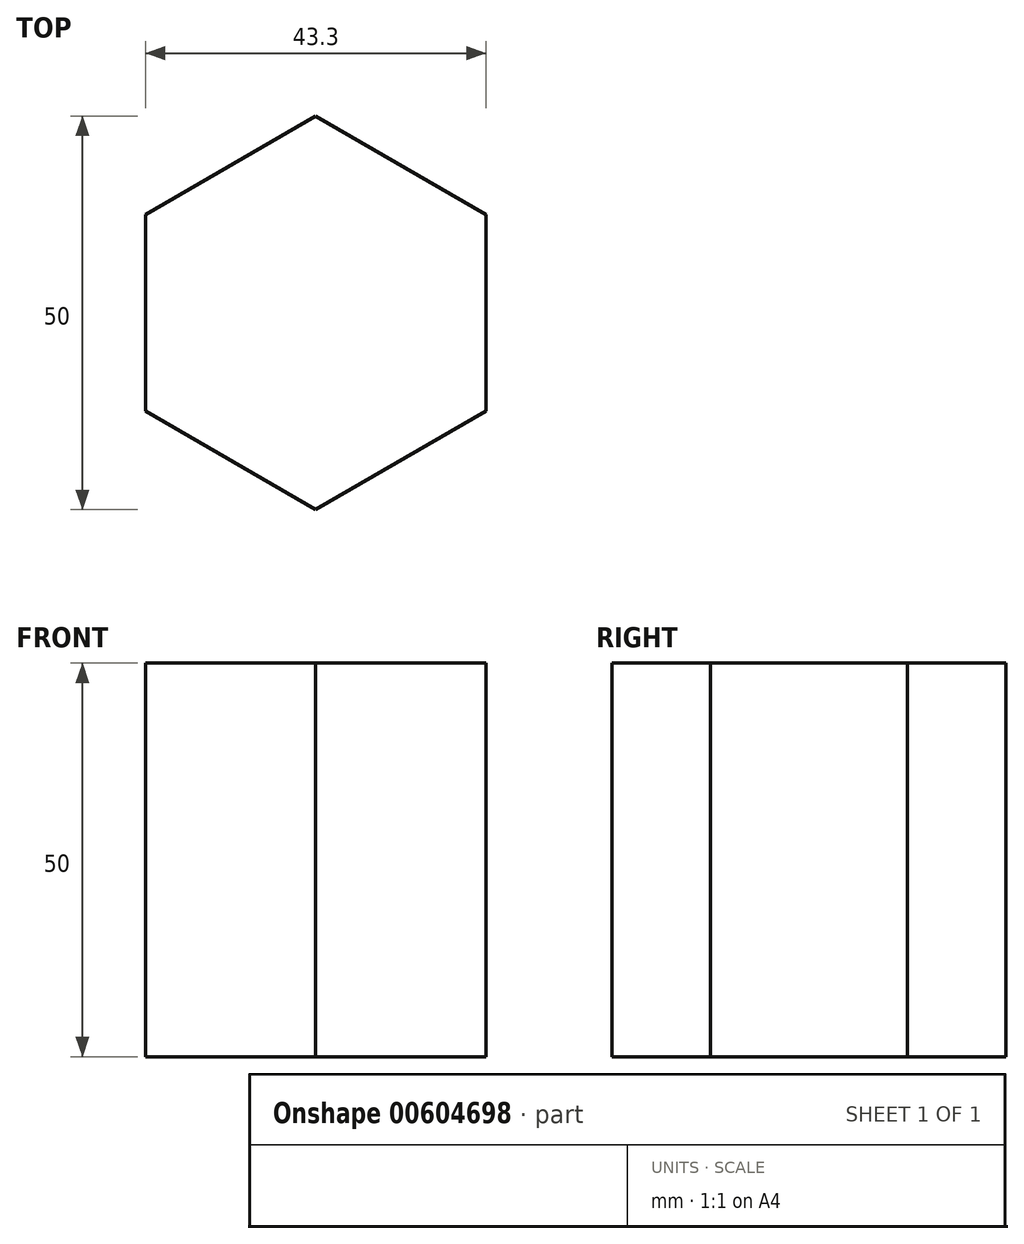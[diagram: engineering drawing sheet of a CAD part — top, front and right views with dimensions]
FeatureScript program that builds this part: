
annotation { "Feature Type Name" : "Feature", "Feature Type Description" : "" }
export const myFeature = defineFeature(function(context is Context, id is Id, definition is map)
    precondition{}
    {
        {
            var Q0;
            Q0=qCreatedBy(makeId("Top.planeOp"),FACE);
            var sketch = newSketch(context, id + "F0", { "sketchPlane" : qUnion([Q0])});
            skCircle(sketch, "E0.cCircle", {"center": v(0, 0) * mm, "radius": 25 * mm, "construction": true});
            skLineSegment(sketch, "E0.0", {"start": v(0, -25) * mm, "end": v(-21.65, -12.5) * mm});
            skLineSegment(sketch, "E0.1", {"start": v(-21.65, -12.5) * mm, "end": v(-21.65, 12.5) * mm});
            skLineSegment(sketch, "E0.2", {"start": v(-21.65, 12.5) * mm, "end": v(0, 25) * mm});
            skLineSegment(sketch, "E0.3", {"start": v(0, 25) * mm, "end": v(21.65, 12.5) * mm});
            skLineSegment(sketch, "E0.4", {"start": v(21.65, 12.5) * mm, "end": v(21.65, -12.5) * mm});
            skLineSegment(sketch, "E0.5", {"start": v(21.65, -12.5) * mm, "end": v(0, -25) * mm});
            skSolve(sketch);
        }
        {
            var Q0;
            Q0 = qSketchRegion(id + "F0", true);
            extrude(context, id + "F1", {"entities" : qUnion([Q0]), "depth" : 50 * mm, "offsetDistance" : 25.4 * mm});
        }
    });
